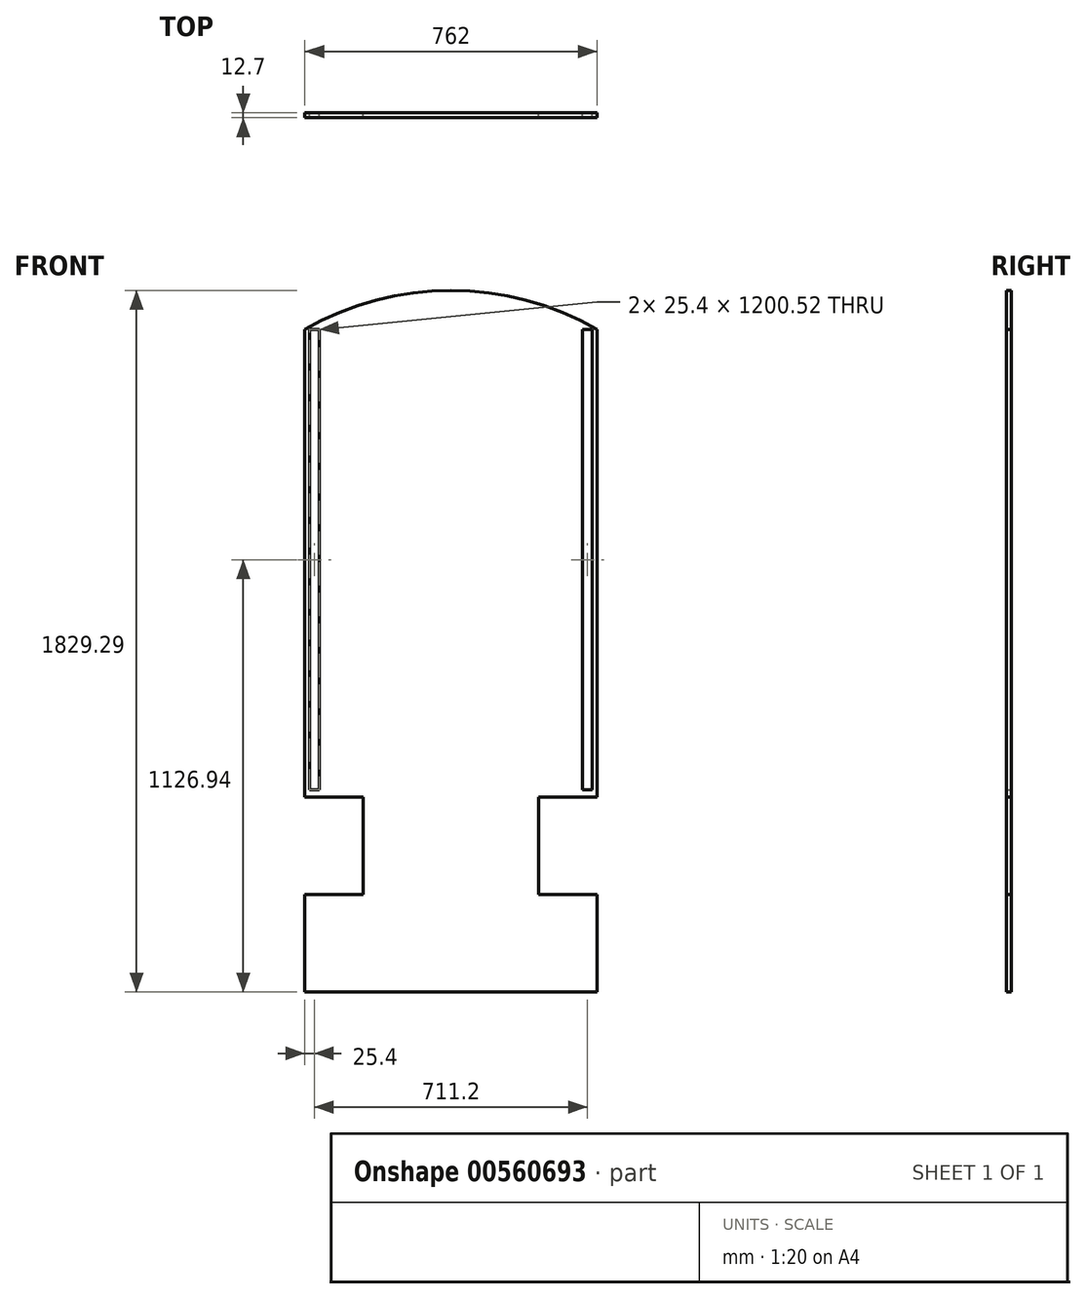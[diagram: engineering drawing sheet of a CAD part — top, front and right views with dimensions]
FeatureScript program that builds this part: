
annotation { "Feature Type Name" : "Feature", "Feature Type Description" : "" }
export const myFeature = defineFeature(function(context is Context, id is Id, definition is map)
    precondition{}
    {
        {
            var Q0;
            Q0=qCreatedBy(makeId("Front.planeOp"),FACE);
            var sketch = newSketch(context, id + "F0", { "sketchPlane" : qUnion([Q0])});
            skLineSegment(sketch, "E0", {"start": v(336.91, 0.2) * mm, "end": v(336.91, -1219) * mm});
            skLineSegment(sketch, "E1", {"start": v(-425.09, 0.2) * mm, "end": v(-425.09, -1219) * mm});
            skPoint(sketch, "E2.visualSharp", {"position": v(-120.29, -1213.02) * mm});
            skPoint(sketch, "E3.visualSharp", {"position": v(32.11, -1213.02) * mm});
            skArc(sketch, "E4", {"start": v(336.91, 0.2) * mm, "mid": v(-44.09, 102.29) * mm, "end": v(-425.09, 0.2) * mm});
            skLineSegment(sketch, "E5.bottom", {"start": v(-412.39, 253.83) * mm, "end": v(-386.99, 253.83) * mm});
            skLineSegment(sketch, "E5.top", {"start": v(-412.39, -1200.32) * mm, "end": v(-386.99, -1200.32) * mm});
            skLineSegment(sketch, "E6.MirrorCS", {"start": v(324.21, 253.83) * mm, "end": v(298.81, 253.83) * mm});
            skLineSegment(sketch, "E7.MirrorCS", {"start": v(324.21, -1200.32) * mm, "end": v(298.81, -1200.32) * mm});
            skPoint(sketch, "E8.orphan", {"position": v(32.11, -1409.87) * mm});
            skPoint(sketch, "E9.start.orphan", {"position": v(-120.29, -1409.87) * mm});
            skLineSegment(sketch, "E10", {"start": v(-425.09, -1219) * mm, "end": v(-272.69, -1219) * mm});
            skLineSegment(sketch, "E11", {"start": v(184.51, -1219) * mm, "end": v(336.91, -1219) * mm});
            skLineSegment(sketch, "E12", {"start": v(-272.69, -1219) * mm, "end": v(-272.69, -1473) * mm});
            skLineSegment(sketch, "E13", {"start": v(-272.69, -1473) * mm, "end": v(-425.09, -1473) * mm});
            skLineSegment(sketch, "E14", {"start": v(-425.09, -1473) * mm, "end": v(-425.09, -1727) * mm});
            skLineSegment(sketch, "E15", {"start": v(-425.09, -1727) * mm, "end": v(336.91, -1727) * mm});
            skLineSegment(sketch, "E16", {"start": v(336.91, -1727) * mm, "end": v(336.91, -1473) * mm});
            skLineSegment(sketch, "E17", {"start": v(336.91, -1473) * mm, "end": v(184.51, -1473) * mm});
            skLineSegment(sketch, "E18", {"start": v(184.51, -1473) * mm, "end": v(184.51, -1219) * mm});
            skLineSegment(sketch, "E19.0", {"start": v(-412.39, 0.2) * mm, "end": v(-412.39, -1200.32) * mm});
            skLineSegment(sketch, "E20", {"start": v(-412.39, 0.2) * mm, "end": v(-386.99, 0.2) * mm});
            skLineSegment(sketch, "E21", {"start": v(-386.99, 0.2) * mm, "end": v(-386.99, -1200.32) * mm});
            skLineSegment(sketch, "E22", {"start": v(-44.09, 102.29) * mm, "end": v(-44.09, -1205.82) * mm});
            skLineSegment(sketch, "E23.MirrorCS", {"start": v(298.81, 0.2) * mm, "end": v(298.81, -1200.32) * mm});
            skLineSegment(sketch, "E24.MirrorCS", {"start": v(324.21, 0.2) * mm, "end": v(324.21, -1200.32) * mm});
            skLineSegment(sketch, "E25.MirrorCS", {"start": v(324.21, 0.2) * mm, "end": v(298.81, 0.2) * mm});
            skSolve(sketch);
        }
        {
            var Q0;
            Q0 = qSketchRegion(id + "F0", true);
            extrude(context, id + "F1", {"entities" : qUnion([Q0]), "depth" : 12.7 * mm, "offsetDistance" : 25.4 * mm});
        }
    });
